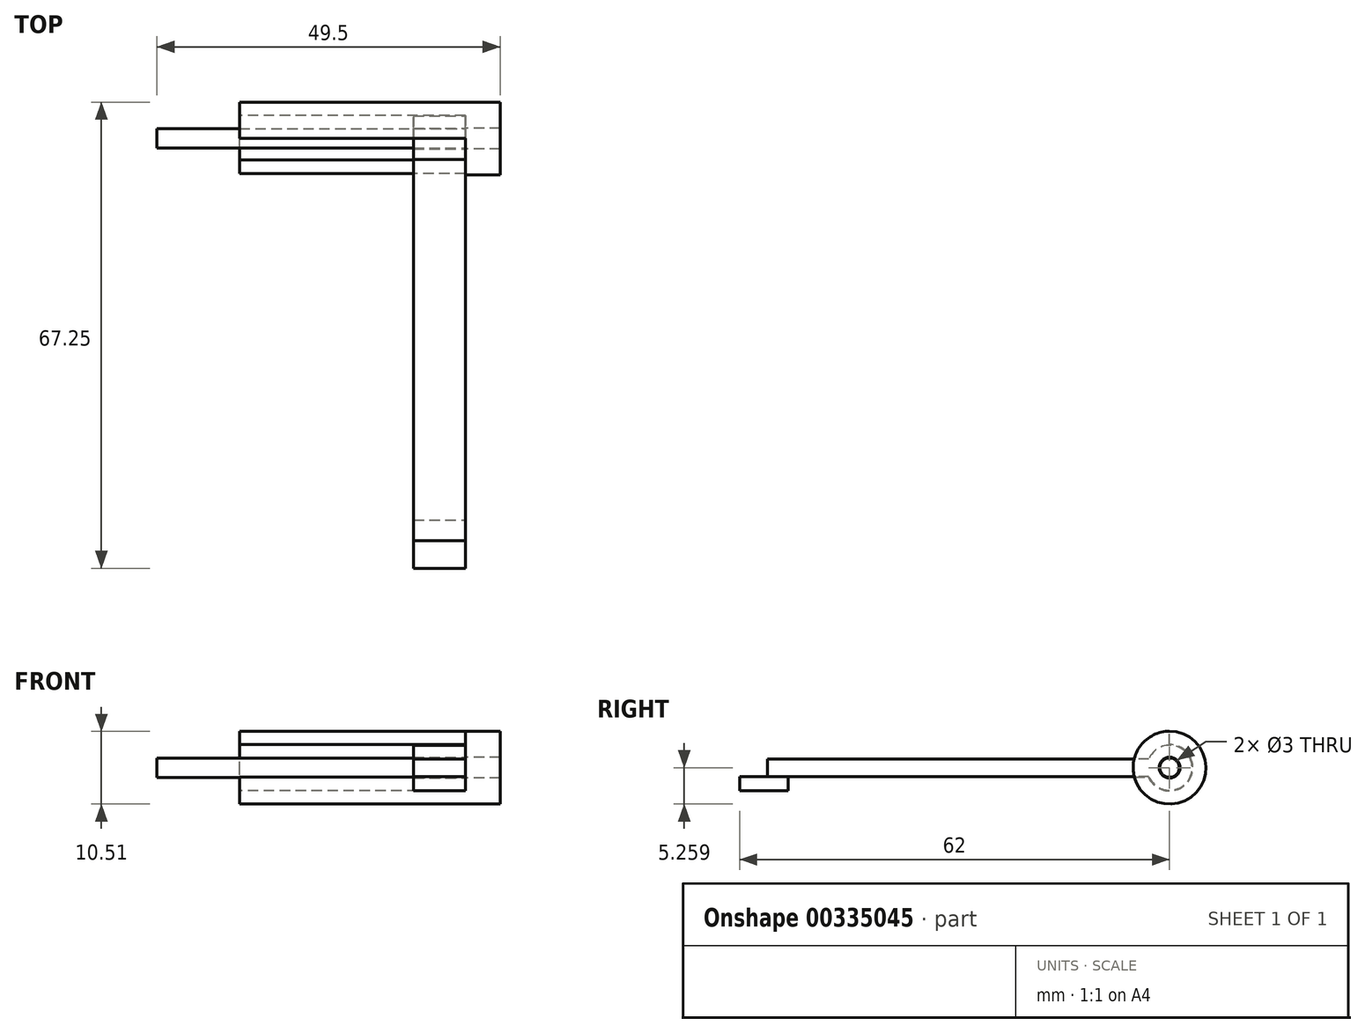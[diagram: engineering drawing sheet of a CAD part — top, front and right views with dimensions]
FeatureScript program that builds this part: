
annotation { "Feature Type Name" : "Feature", "Feature Type Description" : "" }
export const myFeature = defineFeature(function(context is Context, id is Id, definition is map)
    precondition{}
    {
        {
            var Q0;
            Q0=qCreatedBy(makeId("Top.planeOp"),FACE);
            var sketch = newSketch(context, id + "F0", { "sketchPlane" : qUnion([Q0])});
            skLineSegment(sketch, "E0.bottom", {"start": v(8, 0) * mm, "end": v(15.5, 0) * mm});
            skLineSegment(sketch, "E0.top", {"start": v(8, -55) * mm, "end": v(15.5, -55) * mm});
            skLineSegment(sketch, "E0.left", {"start": v(8, 0) * mm, "end": v(8, -55) * mm});
            skLineSegment(sketch, "E0.right", {"start": v(15.5, 0) * mm, "end": v(15.5, -55) * mm});
            skSolve(sketch);
        }
        {
            var Q0;
            Q0=qSketchRegion(id+"F0",true);
            extrude(context, id + "F1", {"entities" : qUnion([Q0]), "depth" : 2.5 * mm});
        }
        {
            var Q0;
            Q0=makeQuery(id+"F1.opExtrude","SWEPT_FACE",FACE,{"disambiguationData":[OSD([sQuery(id+"F0.wireOp",EDGE,"E0.right")])]});
            var sketch = newSketch(context, id + "F2", { "sketchPlane" : qUnion([Q0])});
            skArc(sketch, "E1", {"start": v(-2.07, -0.1) * mm, "mid": v(7.17, -1.93) * mm, "end": v(3, 6.52) * mm});
            skCircle(sketch, "E2", {"center": v(3, 1.27) * mm, "radius": 1.5 * mm});
            skLineSegment(sketch, "E3", {"start": v(0, 2.5) * mm, "end": v(0, 0) * mm});
            skArc(sketch, "E4", {"start": v(0, 0) * mm, "mid": v(6.25, 1.25) * mm, "end": v(0, 2.5) * mm});
            skPoint(sketch, "E5.orphan", {"position": v(1.2, 0) * mm});
            skArc(sketch, "E6", {"start": v(-0.06, -0.1) * mm, "mid": v(5.81, -0.55) * mm, "end": v(3, 4.62) * mm});
            skLineSegment(sketch, "E7", {"start": v(-2.07, -0.1) * mm, "end": v(-0.06, -0.1) * mm});
            skLineSegment(sketch, "E8.trimOffspring", {"start": v(3, 4.62) * mm, "end": v(3, 6.52) * mm});
            skPoint(sketch, "E9.end.orphan", {"position": v(-2.1, 0) * mm});
            skCircle(sketch, "E10", {"center": v(3, 1.27) * mm, "radius": 1.4 * mm});
            skSolve(sketch);
        }
        {
            var Q0;
            Q0=makeQuery(id+"F2.imprint","IMPRINT",FACE,{"disambiguationData":[TD([[makeQuery(id+"F2.imprint","IMPRINT",EDGE,{"derivedFrom":sQuery(id+"F2.wireOp",EDGE,"E2")}),-1.0]])]});
            extrude(context, id + "F3", {"entities" : qUnion([Q0]), "operationType" : NewBodyOperationType.ADD, "oppositeDirection" : true, "depth" : 7.5 * mm});
        }
        {
            var Q0;
            Q0=makeQuery(id+"F2.imprint","IMPRINT",FACE,{"disambiguationData":[TD([[makeQuery(id+"F2.imprint","IMPRINT",EDGE,{"derivedFrom":sQuery(id+"F2.wireOp",EDGE,"E1")}),1.0]])]});
            var sketch = newSketch(context, id + "F4", { "sketchPlane" : qUnion([Q0])});
            skCircle(sketch, "E11", {"center": v(3, 1.27) * mm, "radius": 5.25 * mm});
            skCircle(sketch, "E12", {"center": v(3, 1.27) * mm, "radius": 1.5 * mm});
            skSolve(sketch);
        }
        {
            var Q0;
            Q0=sQuery(id+"F2.wireOp",EDGE,"E10");
            extrude(context, id + "F5", {"bodyType" : ToolBodyType.SURFACE, "surfaceEntities" : qUnion([Q0]), "oppositeDirection" : true, "depth" : 40 * mm});
        }
        {
            var Q0;
            Q0=makeQuery(id+"F2.imprint","IMPRINT",FACE,{"disambiguationData":[TD([[makeQuery(id+"F2.imprint","IMPRINT",EDGE,{"derivedFrom":sQuery(id+"F2.wireOp",EDGE,"E1")}),1.0]])]});
            extrude(context, id + "F6", {"entities" : qUnion([Q0]), "oppositeDirection" : true, "depth" : 16.3 * mm});
        }
        {
            var Q0;
            Q0=makeQuery(id+"F5.opExtrude","SWEPT_BODY",BODY,{"disambiguationData":[OSD([sQuery(id+"F2.wireOp",EDGE,"E10")])]});
            deleteBodies(context, id + "F7", {"entities" : qUnion([Q0])});
        }
        {
            var Q0;
            {var subQ0=sQuery(id+"F0.wireOp",EDGE,"E0.right");var subQ1=makeQuery(id+"F1.opExtrude","CAP_EDGE",EDGE,{"disambiguationData":[OSD([subQ0])],"isStart":true});Q0=makeQuery(id+"F2.imprint","IMPRINT",FACE,{"disambiguationData":[TD([[makeQuery(id+"F2.imprint","IMPRINT",EDGE,{"derivedFrom":subQ1}),-1.0]])]});}
            var sketch = newSketch(context, id + "F8", { "sketchPlane" : qUnion([Q0])});
            skLineSegment(sketch, "E13.bottom", {"start": v(-52, 0) * mm, "end": v(-59, 0) * mm});
            skLineSegment(sketch, "E13.top", {"start": v(-52, -2.05) * mm, "end": v(-59, -2.05) * mm});
            skLineSegment(sketch, "E13.left", {"start": v(-52, 0) * mm, "end": v(-52, -2.05) * mm});
            skLineSegment(sketch, "E13.right", {"start": v(-59, 0) * mm, "end": v(-59, -2.05) * mm});
            skSolve(sketch);
        }
        {
            var Q0;
            Q0=makeQuery(id+"F8.imprint","IMPRINT",FACE,{"disambiguationData":[TD([[makeQuery(id+"F8.imprint","IMPRINT",EDGE,{"derivedFrom":sQuery(id+"F8.wireOp",EDGE,"E13.top")}),-1.0]])]});
            extrude(context, id + "F9", {"entities" : qUnion([Q0]), "depth" : -7.5 * mm});
        }
        {
            var Q0;
            Q0=makeQuery(id+"F2.imprint","IMPRINT",FACE,{"disambiguationData":[TD([[makeQuery(id+"F2.imprint","IMPRINT",EDGE,{"derivedFrom":sQuery(id+"F2.wireOp",EDGE,"E1")}),1.0]])]});
            var sketch = newSketch(context, id + "F10", { "sketchPlane" : qUnion([Q0])});
            skSolve(sketch);
        }
        {
            var Q0;
            Q0 = qSketchRegion(id + "F4", true);
            var Q1;
            Q1=makeQuery(id+"F4.imprint","IMPRINT",FACE,{"disambiguationData":[TD([[makeQuery(id+"F4.imprint","IMPRINT",EDGE,{"derivedFrom":sQuery(id+"F4.wireOp",EDGE,"E12")}),-1.0]])]});
            var Q2;
            Q2=makeQuery(id+"F10.imprint","IMPRINT",FACE,{"disambiguationData":[TD([[makeQuery(id+"F10.imprint","IMPRINT",EDGE,{"derivedFrom":makeQuery(id+"F2.imprint","IMPRINT",EDGE,{"derivedFrom":sQuery(id+"F2.wireOp",EDGE,"E1")})}),1.0]])]});
            extrude(context, id + "F11", {"entities" : qUnion([Q0, Q1, Q2]), "depth" : 5 * mm});
        }
        {
            var Q0;
            Q0=makeQuery(id+"F6.opExtrude","SWEPT_BODY",BODY,{"disambiguationData":[OSD([sQuery(id+"F2.wireOp",EDGE,"E1"),sQuery(id+"F2.wireOp",EDGE,"E6"),sQuery(id+"F2.wireOp",EDGE,"E7"),sQuery(id+"F2.wireOp",EDGE,"E8.trimOffspring")])]});
            var Q1;
            Q1=makeQuery(id+"F6.opExtrude","CAP_FACE",FACE,{"disambiguationData":[OSD([sQuery(id+"F2.wireOp",EDGE,"E1"),sQuery(id+"F2.wireOp",EDGE,"E6"),sQuery(id+"F2.wireOp",EDGE,"E7"),sQuery(id+"F2.wireOp",EDGE,"E8.trimOffspring")])],"isStart":false});
            mirror(context, id + "F12", {"operationType" : NewBodyOperationType.ADD, "entities" : qUnion([Q0]), "mirrorPlane" : qUnion([Q1])});
        }
        {
            var Q0;
            Q0=makeQuery(id+"F2.imprint","IMPRINT",FACE,{"disambiguationData":[TD([[makeQuery(id+"F2.imprint","IMPRINT",EDGE,{"derivedFrom":sQuery(id+"F2.wireOp",EDGE,"E10")}),1.0]])]});
            extrude(context, id + "F13", {"entities" : qUnion([Q0]), "oppositeDirection" : true, "depth" : 44.5 * mm});
        }
    });
